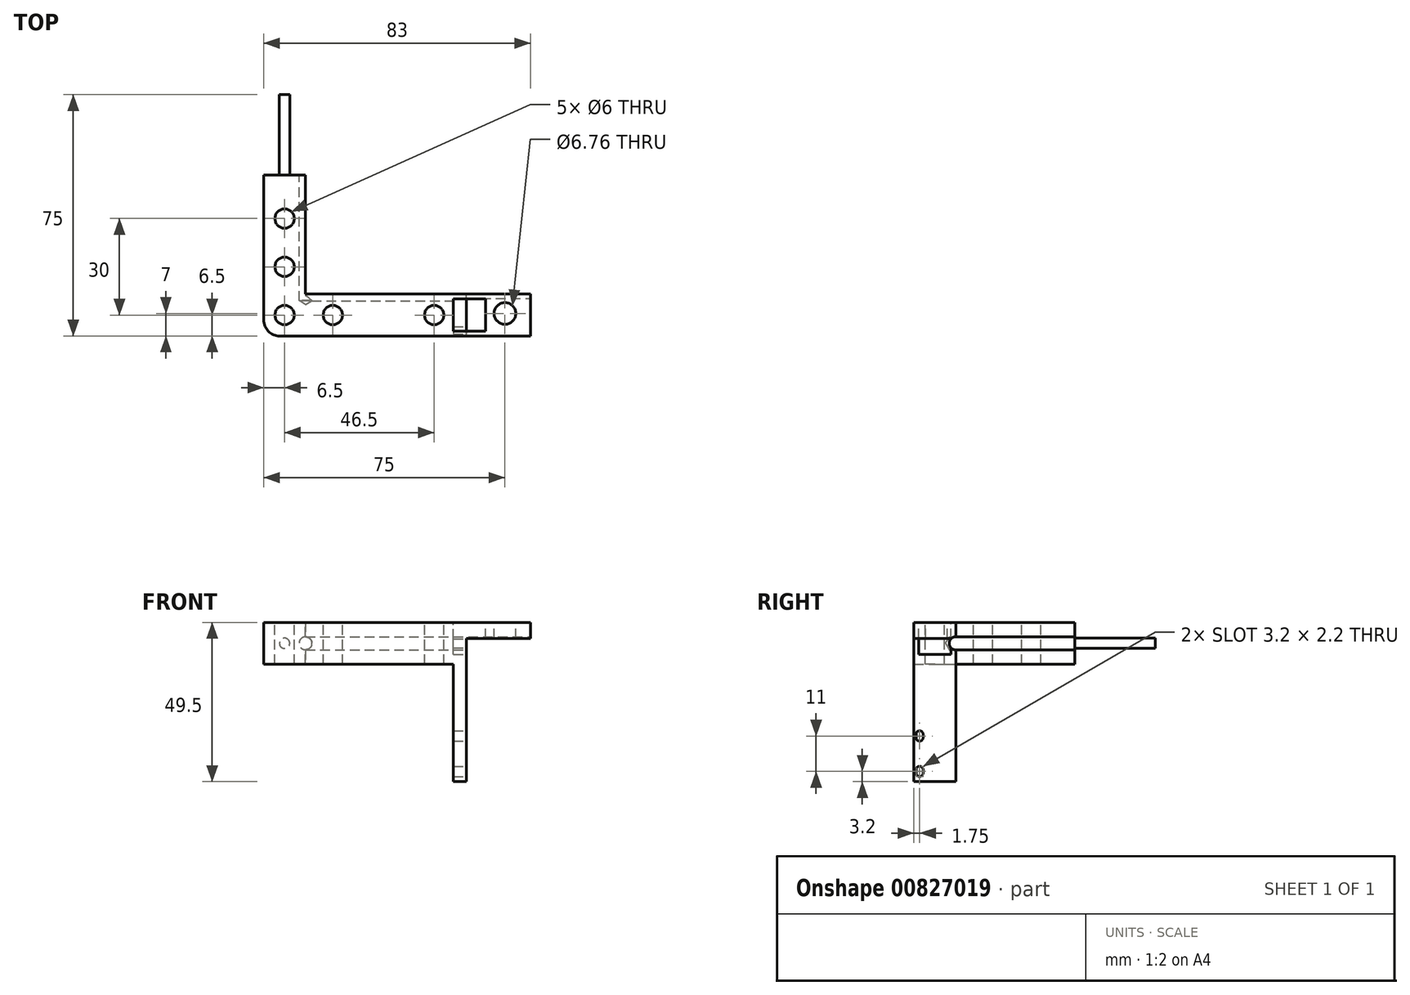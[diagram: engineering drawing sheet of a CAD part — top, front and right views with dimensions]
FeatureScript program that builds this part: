
annotation { "Feature Type Name" : "Feature", "Feature Type Description" : "" }
export const myFeature = defineFeature(function(context is Context, id is Id, definition is map)
    precondition{}
    {
        {
            var Q0;
            Q0=qCreatedBy(makeId("Front.planeOp"),FACE);
            var sketch = newSketch(context, id + "F0", { "sketchPlane" : qUnion([Q0])});
            skLineSegment(sketch, "E0.bottom", {"start": v(6.5, -6.5) * mm, "end": v(-6.5, -6.5) * mm});
            skLineSegment(sketch, "E0.top", {"start": v(6.5, 6.5) * mm, "end": v(-6.5, 6.5) * mm});
            skLineSegment(sketch, "E0.left", {"start": v(6.5, -6.5) * mm, "end": v(6.5, 6.5) * mm});
            skLineSegment(sketch, "E0.right", {"start": v(-6.5, -6.5) * mm, "end": v(-6.5, 6.5) * mm});
            skPoint(sketch, "E0.middle", {"position": v(0, 0) * mm});
            skSolve(sketch);
        }
        {
            var Q0;
            Q0 = qSketchRegion(id + "F0", true);
            extrude(context, id + "F1", {"entities" : qUnion([Q0]), "depth" : 50 * mm, "offsetDistance" : 25 * mm});
        }
        {
            var Q0;
            Q0=makeQuery(id+"F1.opExtrude","SWEPT_FACE",FACE,{"disambiguationData":[OSD([sQuery(id+"F0.wireOp",EDGE,"E0.left")])]});
            var sketch = newSketch(context, id + "F2", { "sketchPlane" : qUnion([Q0])});
            skLineSegment(sketch, "E1.bottom", {"start": v(-50, 6.5) * mm, "end": v(-37, 6.5) * mm});
            skLineSegment(sketch, "E1.top", {"start": v(-50, -6.5) * mm, "end": v(-37, -6.5) * mm});
            skLineSegment(sketch, "E1.left", {"start": v(-50, 6.5) * mm, "end": v(-50, -6.5) * mm});
            skLineSegment(sketch, "E1.right", {"start": v(-37, 6.5) * mm, "end": v(-37, -6.5) * mm});
            skSolve(sketch);
        }
        {
            var Q0;
            Q0 = qSketchRegion(id + "F2", true);
            extrude(context, id + "F3", {"entities" : qUnion([Q0]), "operationType" : NewBodyOperationType.ADD, "depth" : 50 * mm, "offsetDistance" : 25 * mm});
        }
        {
            var Q0;
            Q0=makeQuery(id+"F3.opExtrude","CAP_FACE",FACE,{"disambiguationData":[OSD([sQuery(id+"F2.wireOp",EDGE,"E1.bottom"),sQuery(id+"F2.wireOp",EDGE,"E1.top"),sQuery(id+"F2.wireOp",EDGE,"E1.left"),sQuery(id+"F2.wireOp",EDGE,"E1.right")])],"isStart":false});
            var sketch = newSketch(context, id + "F4", { "sketchPlane" : qUnion([Q0])});
            skPoint(sketch, "E2", {"position": v(-43.5, 0) * mm});
            skPoint(sketch, "E2.positionSnap0", {"position": v(-43.5, 6.5) * mm});
            skSolve(sketch);
        }
        {
            var Q0;
            Q0=makeQuery(id+"F1.opExtrude","CAP_FACE",FACE,{"disambiguationData":[OSD([sQuery(id+"F0.wireOp",EDGE,"E0.bottom"),sQuery(id+"F0.wireOp",EDGE,"E0.top"),sQuery(id+"F0.wireOp",EDGE,"E0.left"),sQuery(id+"F0.wireOp",EDGE,"E0.right")])],"isStart":true});
            var sketch = newSketch(context, id + "F5", { "sketchPlane" : qUnion([Q0])});
            skCircle(sketch, "E3", {"center": v(0, 0) * mm, "radius": 1.6 * mm});
            skSolve(sketch);
        }
        {
            var Q0;
            Q0 = qSketchRegion(id + "F5", true);
            extrude(context, id + "F6", {"entities" : qUnion([Q0]), "operationType" : NewBodyOperationType.ADD, "depth" : 25 * mm, "offsetDistance" : 25 * mm});
        }
        {
            var Q0;
            Q0=makeQuery(id+"F3.boolean.opBoolean","MERGE",FACE,{"derivedFrom":[makeQuery(id+"F1.opExtrude","SWEPT_FACE",FACE,{"disambiguationData":[OSD([sQuery(id+"F0.wireOp",EDGE,"E0.top")])]}),makeQuery(id+"F3.opExtrude","SWEPT_FACE",FACE,{"disambiguationData":[OSD([sQuery(id+"F2.wireOp",EDGE,"E1.bottom")])]})]});
            var sketch = newSketch(context, id + "F7", { "sketchPlane" : qUnion([Q0])});
            skLineSegment(sketch, "E4", {"start": v(56.5, -43.5) * mm, "end": v(-6.5, -43.5) * mm, "construction": true});
            skLineSegment(sketch, "E5", {"start": v(0, -50) * mm, "end": v(0, 0) * mm, "construction": true});
            skPoint(sketch, "E6", {"position": v(15, -43.5) * mm});
            skPoint(sketch, "E7", {"position": v(0, -43.5) * mm});
            skPoint(sketch, "E8", {"position": v(0, -28.5) * mm});
            skPoint(sketch, "E9", {"position": v(0, -13.5) * mm});
            skPoint(sketch, "E10", {"position": v(46.5, -43.5) * mm});
            skSolve(sketch);
        }
        {
            var Q0;
            Q0=sQuery(id+"F7.wireOp",VERTEX,"E8");
            var Q1;
            Q1=sQuery(id+"F7.wireOp",VERTEX,"E9");
            var Q2;
            Q2=sQuery(id+"F7.wireOp",VERTEX,"E7");
            var Q3;
            Q3=sQuery(id+"F7.wireOp",VERTEX,"E6");
            var Q4;
            Q4=sQuery(id+"F7.wireOp",VERTEX,"E10");
            var Q5;
            Q5=makeQuery(id+"F1.opExtrude","SWEPT_BODY",BODY,{"disambiguationData":[OSD([sQuery(id+"F0.wireOp",EDGE,"E0.bottom"),sQuery(id+"F0.wireOp",EDGE,"E0.top"),sQuery(id+"F0.wireOp",EDGE,"E0.left"),sQuery(id+"F0.wireOp",EDGE,"E0.right")])]});
            hole(context, id + "F8", {"style" : HoleStyle.SIMPLE, "endStyle" : HoleEndStyle.THROUGH, "holeDiameter" : 6 * mm, "majorDiameter" : 5 * mm, "isTappedThrough" : true, "tappedDepth" : 12 * mm, "tapClearance" : 3, "startFromSketch" : true, "locations" : qUnion([Q0, Q1, Q2, Q3, Q4]), "scope" : qUnion([Q5])});
        }
        {
            var Q0;
            Q0=makeQuery(id+"F4.imprint","IMPRINT",FACE,{"disambiguationData":[TD([[makeQuery(id+"F4.imprint","IMPRINT",EDGE,{"derivedFrom":makeQuery(id+"F3.opExtrude","CAP_EDGE",EDGE,{"disambiguationData":[OSD([sQuery(id+"F2.wireOp",EDGE,"E1.bottom")])],"isStart":false})}),-1.0]])]});
            var sketch = newSketch(context, id + "F9", { "sketchPlane" : qUnion([Q0])});
            skLineSegment(sketch, "E11.bottom", {"start": v(-50, 6.5) * mm, "end": v(-37, 6.5) * mm});
            skLineSegment(sketch, "E11.top", {"start": v(-50, 1.5) * mm, "end": v(-37, 1.5) * mm});
            skLineSegment(sketch, "E11.left", {"start": v(-50, 6.5) * mm, "end": v(-50, 1.5) * mm});
            skLineSegment(sketch, "E11.right", {"start": v(-37, 6.5) * mm, "end": v(-37, 1.5) * mm});
            skSolve(sketch);
        }
        {
            var Q0;
            Q0 = qSketchRegion(id + "F9", true);
            extrude(context, id + "F10", {"entities" : qUnion([Q0]), "operationType" : NewBodyOperationType.ADD, "depth" : 20 * mm, "offsetDistance" : 25 * mm});
        }
        {
            var Q0;
            Q0=makeQuery(id+"F3.boolean.opBoolean","MERGE",FACE,{"derivedFrom":[makeQuery(id+"F1.opExtrude","SWEPT_FACE",FACE,{"disambiguationData":[OSD([sQuery(id+"F0.wireOp",EDGE,"E0.bottom")])]}),makeQuery(id+"F3.opExtrude","SWEPT_FACE",FACE,{"disambiguationData":[OSD([sQuery(id+"F2.wireOp",EDGE,"E1.top")])]})]});
            var sketch = newSketch(context, id + "F11", { "sketchPlane" : qUnion([Q0])});
            skLineSegment(sketch, "E12.bottom", {"start": v(56.5, 50) * mm, "end": v(52.5, 50) * mm});
            skLineSegment(sketch, "E12.top", {"start": v(56.5, 37) * mm, "end": v(52.5, 37) * mm});
            skLineSegment(sketch, "E12.left", {"start": v(56.5, 50) * mm, "end": v(56.5, 37) * mm});
            skLineSegment(sketch, "E12.right", {"start": v(52.5, 50) * mm, "end": v(52.5, 37) * mm});
            skSolve(sketch);
        }
        {
            var Q0;
            Q0 = qSketchRegion(id + "F11", true);
            extrude(context, id + "F12", {"entities" : qUnion([Q0]), "operationType" : NewBodyOperationType.ADD, "depth" : 36.5 * mm, "offsetDistance" : 25 * mm});
        }
        {
            var Q0;
            Q0=makeQuery(id+"F10.boolean.opBoolean","MERGE",FACE,{"derivedFrom":[makeQuery(id+"F3.boolean.opBoolean","MERGE",FACE,{"derivedFrom":[makeQuery(id+"F1.opExtrude","SWEPT_FACE",FACE,{"disambiguationData":[OSD([sQuery(id+"F0.wireOp",EDGE,"E0.top")])]}),makeQuery(id+"F3.opExtrude","SWEPT_FACE",FACE,{"disambiguationData":[OSD([sQuery(id+"F2.wireOp",EDGE,"E1.bottom")])]})]}),makeQuery(id+"F10.opExtrude","SWEPT_FACE",FACE,{"disambiguationData":[OSD([sQuery(id+"F9.wireOp",EDGE,"E11.bottom")])]})]});
            var sketch = newSketch(context, id + "F13", { "sketchPlane" : qUnion([Q0])});
            skLineSegment(sketch, "E13.bottom", {"start": v(54.96, -37.5) * mm, "end": v(58.56, -37.5) * mm});
            skLineSegment(sketch, "E13.top", {"start": v(54.96, -47.5) * mm, "end": v(58.56, -47.5) * mm});
            skLineSegment(sketch, "E13.left", {"start": v(54.96, -37.5) * mm, "end": v(54.96, -47.5) * mm});
            skLineSegment(sketch, "E13.right", {"start": v(58.56, -37.5) * mm, "end": v(58.56, -47.5) * mm});
            skSolve(sketch);
        }
        {
            var Q0;
            Q0=makeQuery(id+"F10.boolean.opBoolean","MERGE",FACE,{"derivedFrom":[makeQuery(id+"F3.boolean.opBoolean","MERGE",FACE,{"derivedFrom":[makeQuery(id+"F1.opExtrude","SWEPT_FACE",FACE,{"disambiguationData":[OSD([sQuery(id+"F0.wireOp",EDGE,"E0.top")])]}),makeQuery(id+"F3.opExtrude","SWEPT_FACE",FACE,{"disambiguationData":[OSD([sQuery(id+"F2.wireOp",EDGE,"E1.bottom")])]})]}),makeQuery(id+"F10.opExtrude","SWEPT_FACE",FACE,{"disambiguationData":[OSD([sQuery(id+"F9.wireOp",EDGE,"E11.bottom")])]})]});
            var sketch = newSketch(context, id + "F14", { "sketchPlane" : qUnion([Q0])});
            skPoint(sketch, "E14", {"position": v(68.5, -43) * mm});
            skSolve(sketch);
        }
        {
            var Q0;
            Q0=sQuery(id+"F14.wireOp",VERTEX,"E14");
            var Q1;
            Q1=makeQuery(id+"F1.opExtrude","SWEPT_BODY",BODY,{"disambiguationData":[OSD([sQuery(id+"F0.wireOp",EDGE,"E0.bottom"),sQuery(id+"F0.wireOp",EDGE,"E0.top"),sQuery(id+"F0.wireOp",EDGE,"E0.left"),sQuery(id+"F0.wireOp",EDGE,"E0.right")])]});
            hole(context, id + "F15", {"style" : HoleStyle.SIMPLE, "endStyle" : HoleEndStyle.THROUGH, "standardTappedOrClearance" : lookupTablePath({ "fit" : "Normal (ASME)", "standard" : "ANSI", "size" : "1/4", "type" : "Clearance" }), "standardBlindInLast" : lookupTablePath({ "fit" : "Free", "standard" : "ANSI", "size" : "1/4", "type" : "Clearance" }), "holeDiameter" : 6.76 * mm, "majorDiameter" : 5 * mm, "isTappedThrough" : true, "tappedDepth" : 12 * mm, "tapClearance" : 3, "startFromSketch" : true, "locations" : qUnion([Q0]), "scope" : qUnion([Q1])});
        }
        {
            var Q0;
            Q0=makeQuery(id+"F12.boolean.opBoolean","MERGE",FACE,{"derivedFrom":[makeQuery(id+"F3.opExtrude","CAP_FACE",FACE,{"disambiguationData":[OSD([sQuery(id+"F2.wireOp",EDGE,"E1.bottom"),sQuery(id+"F2.wireOp",EDGE,"E1.top"),sQuery(id+"F2.wireOp",EDGE,"E1.left"),sQuery(id+"F2.wireOp",EDGE,"E1.right")])],"isStart":false}),makeQuery(id+"F12.opExtrude","SWEPT_FACE",FACE,{"disambiguationData":[OSD([sQuery(id+"F11.wireOp",EDGE,"E12.left")])]})]});
            var sketch = newSketch(context, id + "F16", { "sketchPlane" : qUnion([Q0])});
            skLineSegment(sketch, "E15", {"start": v(-48.25, -43) * mm, "end": v(-48.25, -14.6) * mm, "construction": true});
            skPoint(sketch, "E16", {"position": v(-48.25, -28.8) * mm});
            skPoint(sketch, "E17", {"position": v(-48.25, -39.8) * mm});
            skArc(sketch, "E18", {"start": v(-49.35, -40.3) * mm, "mid": v(-48.25, -41.4) * mm, "end": v(-47.15, -40.3) * mm});
            skArc(sketch, "E19", {"start": v(-47.15, -39.3) * mm, "mid": v(-48.25, -38.2) * mm, "end": v(-49.35, -39.3) * mm});
            skLineSegment(sketch, "E20", {"start": v(-49.35, -39.3) * mm, "end": v(-49.35, -40.3) * mm});
            skLineSegment(sketch, "E21", {"start": v(-47.15, -39.3) * mm, "end": v(-47.15, -40.3) * mm});
            skArc(sketch, "E22.0.1.0", {"start": v(-49.35, -29.3) * mm, "mid": v(-48.25, -30.4) * mm, "end": v(-47.15, -29.3) * mm});
            skLineSegment(sketch, "E22.0.1.1", {"start": v(-49.35, -28.3) * mm, "end": v(-49.35, -29.3) * mm});
            skArc(sketch, "E22.0.1.2", {"start": v(-47.15, -28.3) * mm, "mid": v(-48.25, -27.2) * mm, "end": v(-49.35, -28.3) * mm});
            skLineSegment(sketch, "E22.0.1.3", {"start": v(-47.15, -28.3) * mm, "end": v(-47.15, -29.3) * mm});
            skLineSegment(sketch, "E22.0.1.4", {"start": v(-48.25, -32) * mm, "end": v(-48.25, -3.6) * mm, "construction": true});
            skLineSegment(sketch, "E22.direction1", {"start": v(-48.25, -43) * mm, "end": v(-23.25, -43) * mm, "construction": true});
            skLineSegment(sketch, "E22.direction2", {"start": v(-48.25, -43) * mm, "end": v(-48.25, -32) * mm, "construction": true});
            skSolve(sketch);
        }
        {
            var Q0;
            Q0=makeQuery(id+"F16.imprint","IMPRINT",FACE,{"disambiguationData":[TD([[makeQuery(id+"F16.imprint","IMPRINT",EDGE,{"derivedFrom":sQuery(id+"F16.wireOp",EDGE,"E18")}),1.0]])]});
            var Q1;
            Q1=makeQuery(id+"F16.imprint","IMPRINT",FACE,{"disambiguationData":[TD([[makeQuery(id+"F16.imprint","IMPRINT",EDGE,{"derivedFrom":sQuery(id+"F16.wireOp",EDGE,"E22.0.1.0")}),1.0]])]});
            extrude(context, id + "F17", {"entities" : qUnion([Q0, Q1]), "operationType" : NewBodyOperationType.REMOVE, "endBound" : BoundingType.UP_TO_NEXT, "oppositeDirection" : true, "depth" : 25 * mm, "offsetDistance" : 25 * mm});
        }
        {
            var Q0;
            Q0=makeQuery(id+"F10.boolean.opBoolean","MERGE",FACE,{"derivedFrom":[makeQuery(id+"F3.boolean.opBoolean","MERGE",FACE,{"derivedFrom":[makeQuery(id+"F1.opExtrude","SWEPT_FACE",FACE,{"disambiguationData":[OSD([sQuery(id+"F0.wireOp",EDGE,"E0.top")])]}),makeQuery(id+"F3.opExtrude","SWEPT_FACE",FACE,{"disambiguationData":[OSD([sQuery(id+"F2.wireOp",EDGE,"E1.bottom")])]})]}),makeQuery(id+"F10.opExtrude","SWEPT_FACE",FACE,{"disambiguationData":[OSD([sQuery(id+"F9.wireOp",EDGE,"E11.bottom")])]})]});
            var sketch = newSketch(context, id + "F18", { "sketchPlane" : qUnion([Q0])});
            skLineSegment(sketch, "E23.bottom", {"start": v(52.5, -38.5) * mm, "end": v(62.5, -38.5) * mm});
            skLineSegment(sketch, "E23.top", {"start": v(52.5, -48.5) * mm, "end": v(62.5, -48.5) * mm});
            skLineSegment(sketch, "E23.left", {"start": v(52.5, -38.5) * mm, "end": v(52.5, -48.5) * mm});
            skLineSegment(sketch, "E23.right", {"start": v(62.5, -38.5) * mm, "end": v(62.5, -48.5) * mm});
            skSolve(sketch);
        }
        {
            var Q0;
            Q0=makeQuery(id+"F18.imprint","IMPRINT",FACE,{"disambiguationData":[TD([[makeQuery(id+"F18.imprint","IMPRINT",EDGE,{"derivedFrom":sQuery(id+"F18.wireOp",EDGE,"E23.bottom")}),-1.0]])]});
            extrude(context, id + "F19", {"entities" : qUnion([Q0]), "operationType" : NewBodyOperationType.REMOVE, "oppositeDirection" : true, "depth" : 10 * mm, "offsetDistance" : 25 * mm});
        }
        {
            var Q0;
            Q0=makeQuery(id+"F1.opExtrude","CAP_FACE",FACE,{"disambiguationData":[OSD([sQuery(id+"F0.wireOp",EDGE,"E0.bottom"),sQuery(id+"F0.wireOp",EDGE,"E0.top"),sQuery(id+"F0.wireOp",EDGE,"E0.left"),sQuery(id+"F0.wireOp",EDGE,"E0.right")])],"isStart":true});
            var sketch = newSketch(context, id + "F20", { "sketchPlane" : qUnion([Q0])});
            skPoint(sketch, "E24", {"position": v(-6.5, 0) * mm});
            skSolve(sketch);
        }
        {
            var Q0;
            Q0=makeQuery(id+"F10.opExtrude","CAP_FACE",FACE,{"disambiguationData":[OSD([sQuery(id+"F9.wireOp",EDGE,"E11.bottom"),sQuery(id+"F9.wireOp",EDGE,"E11.top"),sQuery(id+"F9.wireOp",EDGE,"E11.left"),sQuery(id+"F9.wireOp",EDGE,"E11.right")])],"isStart":false});
            var sketch = newSketch(context, id + "F21", { "sketchPlane" : qUnion([Q0])});
            skCircle(sketch, "E25", {"center": v(-327.08, 0) * mm, "radius": 1.75 * mm});
            skPoint(sketch, "E26", {"position": v(-37, 0) * mm});
            skSolve(sketch);
        }
        {
            var Q0;
            Q0=makeQuery(id+"F1.opExtrude","CAP_EDGE",EDGE,{"disambiguationData":[OSD([sQuery(id+"F0.wireOp",EDGE,"E0.right")])],"isStart":false});
            fillet(context, id + "F22", {"entities" : qUnion([Q0]), "radius" : 5 * mm, "tangentPropagation" : true, "allowEdgeOverflow" : false});
        }
        {
            var Q0;
            Q0=sQuery(id+"F20.wireOp",VERTEX,"E24");
            var Q1;
            Q1=makeQuery(id+"F1.opExtrude","SWEPT_BODY",BODY,{"disambiguationData":[OSD([sQuery(id+"F0.wireOp",EDGE,"E0.bottom"),sQuery(id+"F0.wireOp",EDGE,"E0.top"),sQuery(id+"F0.wireOp",EDGE,"E0.left"),sQuery(id+"F0.wireOp",EDGE,"E0.right")])]});
            hole(context, id + "F23", {"style" : HoleStyle.SIMPLE, "endStyle" : HoleEndStyle.BLIND, "holeDiameter" : 4 * mm, "majorDiameter" : 5 * mm, "holeDepth" : 39 * mm, "isTappedThrough" : true, "tappedDepth" : 12 * mm, "tapClearance" : 3, "startFromSketch" : true, "locations" : qUnion([Q0]), "scope" : qUnion([Q1])});
        }
        {
            var Q0;
            Q0=sQuery(id+"F21.wireOp",VERTEX,"E26");
            var Q1;
            Q1=makeQuery(id+"F1.opExtrude","SWEPT_BODY",BODY,{"disambiguationData":[OSD([sQuery(id+"F0.wireOp",EDGE,"E0.bottom"),sQuery(id+"F0.wireOp",EDGE,"E0.top"),sQuery(id+"F0.wireOp",EDGE,"E0.left"),sQuery(id+"F0.wireOp",EDGE,"E0.right")])]});
            hole(context, id + "F24", {"style" : HoleStyle.SIMPLE, "endStyle" : HoleEndStyle.BLIND, "holeDiameter" : 4.1 * mm, "majorDiameter" : 5 * mm, "holeDepth" : 70 * mm, "isTappedThrough" : true, "tappedDepth" : 12 * mm, "tapClearance" : 3, "startFromSketch" : true, "locations" : qUnion([Q0]), "scope" : qUnion([Q1])});
        }
    });
